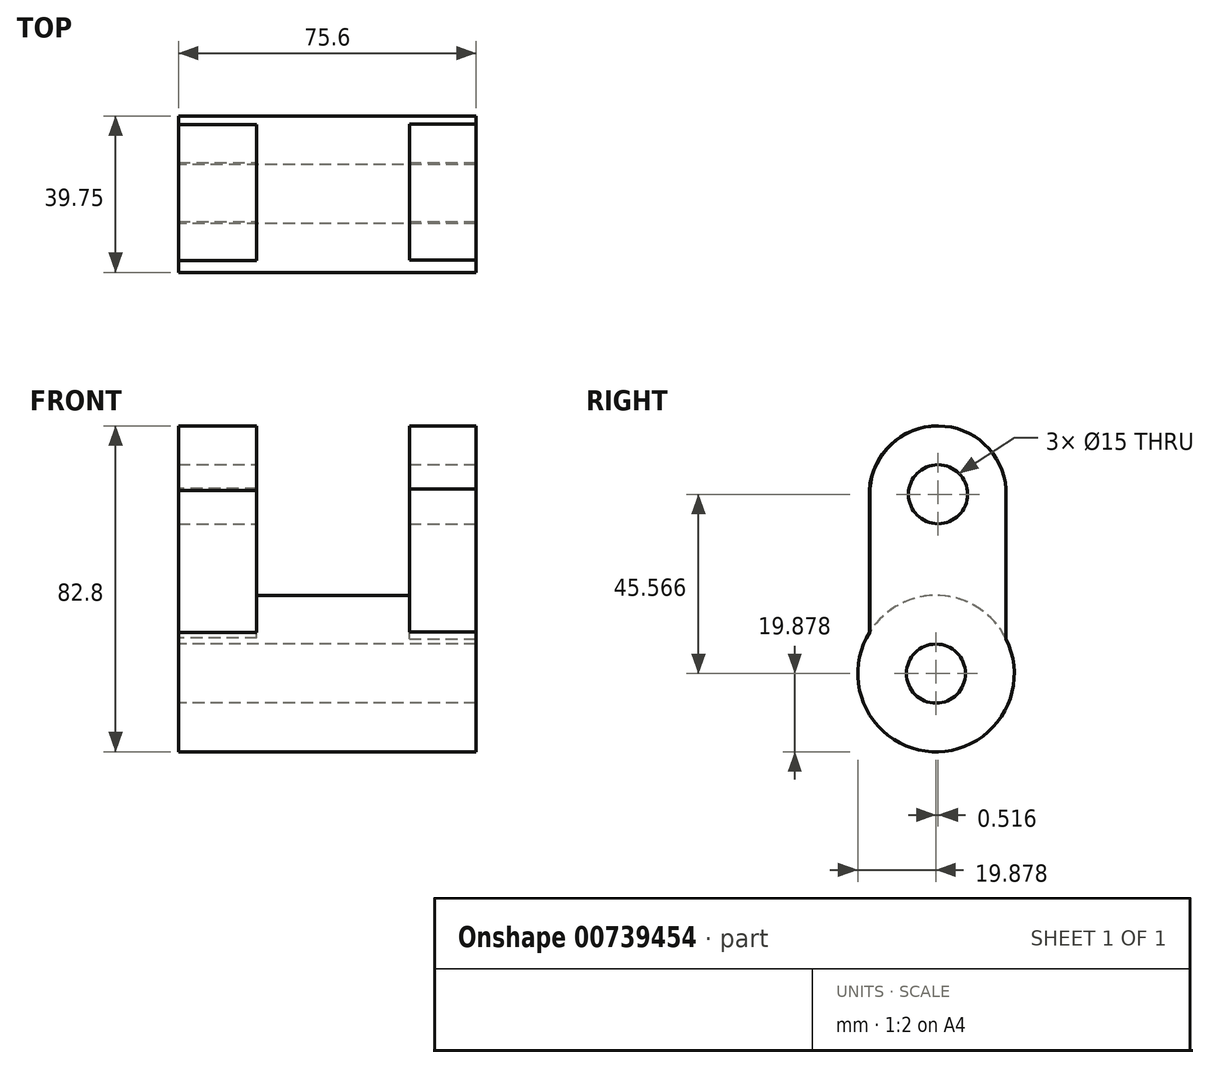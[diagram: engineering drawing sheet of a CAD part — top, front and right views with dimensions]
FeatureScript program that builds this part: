
annotation { "Feature Type Name" : "Feature", "Feature Type Description" : "" }
export const myFeature = defineFeature(function(context is Context, id is Id, definition is map)
    precondition{}
    {
        {
            var Q0;
            Q0=qCreatedBy(makeId("Right.planeOp"),FACE);
            var sketch = newSketch(context, id + "F0", { "sketchPlane" : qUnion([Q0])});
            skCircle(sketch, "E0", {"center": v(-43.25, 28.87) * mm, "radius": 19.87 * mm});
            skSolve(sketch);
        }
        {
            var Q0;
            Q0=makeQuery(id+"F0.imprint","IMPRINT",FACE,{"disambiguationData":[TD([[makeQuery(id+"F0.imprint","IMPRINT",EDGE,{"derivedFrom":sQuery(id+"F0.wireOp",EDGE,"E0")}),1.0]])]});
            extrude(context, id + "F1", {"entities" : qUnion([Q0]), "depth" : 37.1 * mm, "offsetDistance" : 25 * mm, "hasSecondDirection" : true, "secondDirectionOppositeDirection" : true, "secondDirectionDepth" : 38.5 * mm});
        }
        {
            var Q0;
            Q0=makeQuery(id+"F1.opExtrude","CAP_FACE",FACE,{"disambiguationData":[OSD([sQuery(id+"F0.wireOp",EDGE,"E0")])],"isStart":true});
            var sketch = newSketch(context, id + "F2", { "sketchPlane" : qUnion([Q0])});
            skPoint(sketch, "E1", {"position": v(43.25, 28.87) * mm});
            skSolve(sketch);
        }
        {
            var Q0;
            Q0=sQuery(id+"F2.wireOp",VERTEX,"E1");
            var Q1;
            Q1=makeQuery(id+"F1.opExtrude","SWEPT_BODY",BODY,{"disambiguationData":[OSD([sQuery(id+"F0.wireOp",EDGE,"E0")])]});
            hole(context, id + "F3", {"style" : HoleStyle.SIMPLE, "endStyle" : HoleEndStyle.THROUGH, "holeDiameter" : 15 * mm, "majorDiameter" : 5 * mm, "isTappedThrough" : true, "tappedDepth" : 12 * mm, "tapClearance" : 3, "locations" : qUnion([Q0]), "scope" : qUnion([Q1])});
        }
        {
            var Q0;
            Q0=makeQuery(id+"F1.opExtrude","CAP_FACE",FACE,{"disambiguationData":[OSD([sQuery(id+"F0.wireOp",EDGE,"E0")])],"isStart":true});
            var sketch = newSketch(context, id + "F4", { "sketchPlane" : qUnion([Q0])});
            skLineSegment(sketch, "E2.bottom", {"start": v(25.53, 37.87) * mm, "end": v(60.15, 37.87) * mm});
            skLineSegment(sketch, "E2.top", {"start": v(25.53, 93) * mm, "end": v(60.15, 93) * mm});
            skLineSegment(sketch, "E2.left", {"start": v(25.53, 37.87) * mm, "end": v(25.53, 93) * mm});
            skLineSegment(sketch, "E2.right", {"start": v(60.15, 37.87) * mm, "end": v(60.15, 93) * mm});
            skSolve(sketch);
        }
        {
            var Q0;
            Q0=makeQuery(id+"F1.opExtrude","CAP_FACE",FACE,{"disambiguationData":[OSD([sQuery(id+"F0.wireOp",EDGE,"E0")])],"isStart":false});
            var sketch = newSketch(context, id + "F5", { "sketchPlane" : qUnion([Q0])});
            skLineSegment(sketch, "E3.bottom", {"start": v(-25.43, 37.66) * mm, "end": v(-60.04, 37.66) * mm});
            skLineSegment(sketch, "E3.top", {"start": v(-25.43, 92.8) * mm, "end": v(-60.04, 92.8) * mm});
            skLineSegment(sketch, "E3.left", {"start": v(-25.43, 37.66) * mm, "end": v(-25.43, 92.8) * mm});
            skLineSegment(sketch, "E3.right", {"start": v(-60.04, 37.66) * mm, "end": v(-60.04, 92.8) * mm});
            skSolve(sketch);
        }
        {
            var Q0;
            {var subQ0=sQuery(id+"F4.wireOp",EDGE,"E2.top");Q0=makeQuery(id+"F4.imprint","IMPRINT",FACE,{"disambiguationData":[TD([[makeQuery(id+"F4.imprint","IMPRINT",EDGE,{"derivedFrom":subQ0}),-1.0]])]});}
            extrude(context, id + "F6", {"entities" : qUnion([Q0]), "operationType" : NewBodyOperationType.ADD, "oppositeDirection" : true, "depth" : 19.87 * mm, "offsetDistance" : 25 * mm});
        }
        {
            var Q0;
            {var subQ0=sQuery(id+"F5.wireOp",EDGE,"E3.top");Q0=makeQuery(id+"F5.imprint","IMPRINT",FACE,{"disambiguationData":[TD([[makeQuery(id+"F5.imprint","IMPRINT",EDGE,{"derivedFrom":subQ0}),1.0]])]});}
            extrude(context, id + "F7", {"entities" : qUnion([Q0]), "operationType" : NewBodyOperationType.ADD, "oppositeDirection" : true, "depth" : 16.92 * mm, "offsetDistance" : 25 * mm});
        }
        {
            var Q0;
            {var subQ0=sQuery(id+"F0.wireOp",EDGE,"E0");Q0=makeQuery(id+"F6.boolean.opBoolean","MERGE",FACE,{"derivedFrom":[makeQuery(id+"F1.opExtrude","CAP_FACE",FACE,{"disambiguationData":[OSD([subQ0])],"isStart":true}),makeQuery(id+"F6.opExtrude","CAP_FACE",FACE,{"disambiguationData":[OSD([subQ0,sQuery(id+"F4.wireOp",EDGE,"E2.top"),sQuery(id+"F4.wireOp",EDGE,"E2.left"),sQuery(id+"F4.wireOp",EDGE,"E2.right")])],"isStart":true})]});}
            var sketch = newSketch(context, id + "F8", { "sketchPlane" : qUnion([Q0])});
            skArc(sketch, "E4", {"start": v(60.15, 73.42) * mm, "mid": v(42.58, 91.79) * mm, "end": v(25.53, 72.93) * mm});
            skSolve(sketch);
        }
        {
            var Q0;
            {var subQ5=makeQuery(id+"F6.opExtrude","CAP_EDGE",EDGE,{"disambiguationData":[OSD([sQuery(id+"F4.wireOp",EDGE,"E2.top")])],"isStart":true});Q0=makeQuery(id+"F8.imprint","IMPRINT",FACE,{"disambiguationData":[TD([[makeQuery(id+"F8.imprint","IMPRINT",EDGE,{"derivedFrom":subQ5}),-1.0]])]});}
            extrude(context, id + "F9", {"entities" : qUnion([Q0]), "operationType" : NewBodyOperationType.REMOVE, "oppositeDirection" : true, "depth" : 25 * mm, "offsetDistance" : 25 * mm});
        }
        {
            var Q0;
            Q0=makeQuery(id+"F7.opExtrude","CAP_FACE",FACE,{"disambiguationData":[OSD([sQuery(id+"F0.wireOp",EDGE,"E0"),sQuery(id+"F5.wireOp",EDGE,"E3.top"),sQuery(id+"F5.wireOp",EDGE,"E3.left"),sQuery(id+"F5.wireOp",EDGE,"E3.right")])],"isStart":false});
            var sketch = newSketch(context, id + "F10", { "sketchPlane" : qUnion([Q0])});
            skArc(sketch, "E5", {"start": v(60.04, 75.8) * mm, "mid": v(42.7, 91.79) * mm, "end": v(25.43, 75.7) * mm});
            skSolve(sketch);
        }
        {
            var Q0;
            {var subQ0=sQuery(id+"F10.wireOp",EDGE,"E5");Q0=makeQuery(id+"F10.imprint","IMPRINT",FACE,{"disambiguationData":[TD([[makeQuery(id+"F10.imprint","IMPRINT",EDGE,{"derivedFrom":subQ0}),-1.0]])]});}
            extrude(context, id + "F11", {"entities" : qUnion([Q0]), "operationType" : NewBodyOperationType.REMOVE, "oppositeDirection" : true, "depth" : 25 * mm, "offsetDistance" : 25 * mm});
        }
        {
            var Q0;
            {var subQ0=sQuery(id+"F0.wireOp",EDGE,"E0");Q0=makeQuery(id+"F7.boolean.opBoolean","MERGE",FACE,{"derivedFrom":[makeQuery(id+"F1.opExtrude","CAP_FACE",FACE,{"disambiguationData":[OSD([subQ0])],"isStart":false}),makeQuery(id+"F7.opExtrude","CAP_FACE",FACE,{"disambiguationData":[OSD([subQ0,sQuery(id+"F5.wireOp",EDGE,"E3.top"),sQuery(id+"F5.wireOp",EDGE,"E3.left"),sQuery(id+"F5.wireOp",EDGE,"E3.right")])],"isStart":true})]});}
            var sketch = newSketch(context, id + "F12", { "sketchPlane" : qUnion([Q0])});
            skPoint(sketch, "E6", {"position": v(-42.74, 74.43) * mm});
            skSolve(sketch);
        }
        {
            var Q0;
            Q0=sQuery(id+"F12.wireOp",VERTEX,"E6");
            var Q1;
            Q1=makeQuery(id+"F1.opExtrude","SWEPT_BODY",BODY,{"disambiguationData":[OSD([sQuery(id+"F0.wireOp",EDGE,"E0")])]});
            hole(context, id + "F13", {"style" : HoleStyle.SIMPLE, "endStyle" : HoleEndStyle.THROUGH, "holeDiameter" : 15 * mm, "majorDiameter" : 5 * mm, "isTappedThrough" : true, "tappedDepth" : 12 * mm, "tapClearance" : 3, "locations" : qUnion([Q0]), "scope" : qUnion([Q1])});
        }
    });
